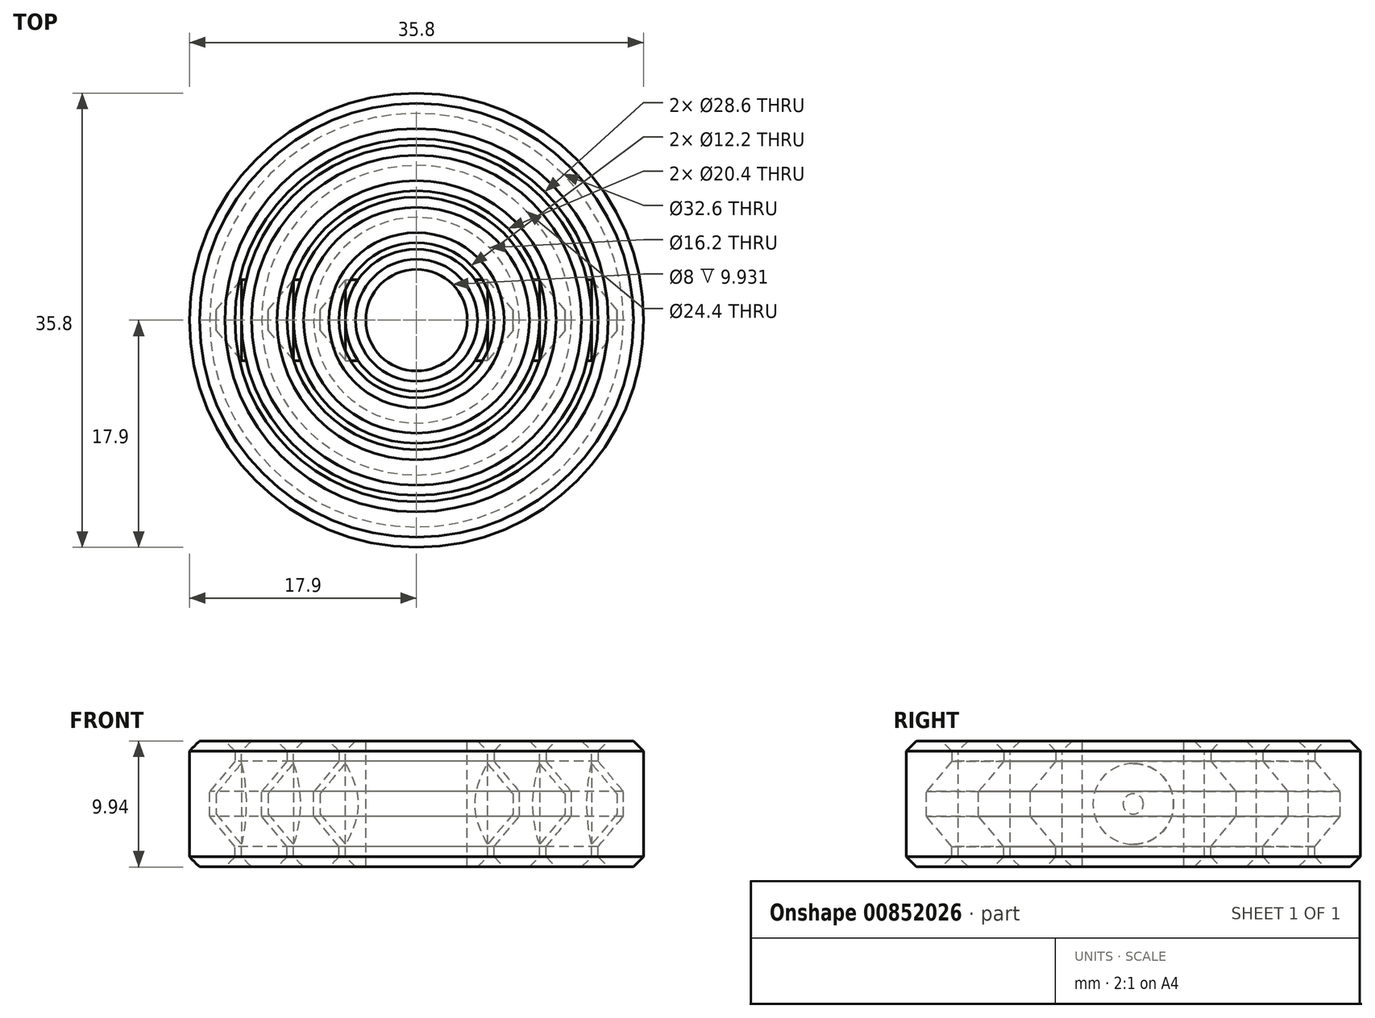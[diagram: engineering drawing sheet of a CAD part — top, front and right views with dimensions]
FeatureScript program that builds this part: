
annotation { "Feature Type Name" : "Feature", "Feature Type Description" : "" }
export const myFeature = defineFeature(function(context is Context, id is Id, definition is map)
    precondition{}
    {
        {
            assignVariable(context, id + "F0", {"name" : "Extrusion", "anyValue" : 0.4});
        }
        {
            assignVariable(context, id + "F1", {"name" : "Shells", "anyValue" : 2});
        }
        {
            assignVariable(context, id + "F2", {"name" : "MinStruct", "anyValue" : getVariable(context, 'Extrusion') * getVariable(context, 'Shells')});
        }
        {
            var Q0;
            Q0=qCreatedBy(makeId("Front.planeOp"),FACE);
            var sketch = newSketch(context, id + "F3", { "sketchPlane" : qUnion([Q0])});
            skLineSegment(sketch, "E0", {"start": v(0, 0) * mm, "end": v(0, -4.97) * mm});
            skLineSegment(sketch, "E1", {"start": v(0, -4.97) * mm, "end": v(5.6, -4.97) * mm});
            skLineSegment(sketch, "E2", {"start": v(5.6, -4.97) * mm, "end": v(5.6, 0) * mm});
            skLineSegment(sketch, "E3", {"start": v(5.6, 0) * mm, "end": v(0, 0) * mm});
            skLineSegment(sketch, "E4", {"start": v(5.6, -3.18) * mm, "end": v(7.6, -0.8) * mm});
            skLineSegment(sketch, "E5", {"start": v(7.6, -0.8) * mm, "end": v(7.6, 0) * mm});
            skLineSegment(sketch, "E6", {"start": v(7.6, 0) * mm, "end": v(5.6, 0) * mm});
            skLineSegment(sketch, "E7", {"start": v(6.1, -4.97) * mm, "end": v(6.1, -3.37) * mm});
            skLineSegment(sketch, "E8", {"start": v(6.1, -3.37) * mm, "end": v(8.1, -0.98) * mm});
            skLineSegment(sketch, "E9", {"start": v(8.1, -0.98) * mm, "end": v(8.1, 0) * mm});
            skLineSegment(sketch, "E10", {"start": v(8.1, 0) * mm, "end": v(9.7, 0) * mm});
            skLineSegment(sketch, "E11", {"start": v(9.7, 0) * mm, "end": v(9.7, -4.97) * mm});
            skLineSegment(sketch, "E12", {"start": v(9.7, -4.97) * mm, "end": v(6.1, -4.97) * mm});
            skLineSegment(sketch, "E13", {"start": v(4, -4.97) * mm, "end": v(4, 0) * mm});
            skLineSegment(sketch, "E14", {"start": v(9.7, -3.18) * mm, "end": v(11.7, -0.8) * mm});
            skLineSegment(sketch, "E15", {"start": v(11.7, -0.8) * mm, "end": v(11.7, 0) * mm});
            skLineSegment(sketch, "E16", {"start": v(11.7, 0) * mm, "end": v(9.7, 0) * mm});
            skArc(sketch, "E17", {"start": v(6.1, -7.54) * mm, "mid": v(8.75, -4.18) * mm, "end": v(9.7, 0) * mm});
            skPoint(sketch, "E18", {"position": v(6.1, -4.17) * mm});
            skArc(sketch, "E19", {"start": v(4, -3.92) * mm, "mid": v(5.18, -2.12) * mm, "end": v(5.6, 0) * mm});
            skLineSegment(sketch, "E20", {"start": v(5.6, -3.18) * mm, "end": v(4, -3.18) * mm});
            skLineSegment(sketch, "E21", {"start": v(9.7, -3.18) * mm, "end": v(9.16, -3.18) * mm});
            skLineSegment(sketch, "E22.1.0.0", {"start": v(15.8, 0) * mm, "end": v(13.8, 0) * mm});
            skLineSegment(sketch, "E22.1.0.1", {"start": v(15.8, -0.8) * mm, "end": v(15.8, 0) * mm});
            skLineSegment(sketch, "E22.1.0.2", {"start": v(13.8, -3.18) * mm, "end": v(15.8, -0.8) * mm});
            skLineSegment(sketch, "E22.1.0.3", {"start": v(13.8, 0) * mm, "end": v(13.8, -4.97) * mm});
            skLineSegment(sketch, "E22.1.0.4", {"start": v(13.8, -4.97) * mm, "end": v(10.2, -4.97) * mm});
            skLineSegment(sketch, "E22.1.0.5", {"start": v(10.2, -4.97) * mm, "end": v(10.2, -3.37) * mm});
            skLineSegment(sketch, "E22.1.0.6", {"start": v(10.2, -3.37) * mm, "end": v(12.2, -0.98) * mm});
            skLineSegment(sketch, "E22.1.0.7", {"start": v(12.2, -0.98) * mm, "end": v(12.2, 0) * mm});
            skLineSegment(sketch, "E22.1.0.8", {"start": v(12.2, 0) * mm, "end": v(13.8, 0) * mm});
            skLineSegment(sketch, "E22.2.0.0", {"start": v(19.9, 0) * mm, "end": v(17.9, 0) * mm});
            skLineSegment(sketch, "E22.2.0.1", {"start": v(19.9, -0.8) * mm, "end": v(19.9, 0) * mm});
            skLineSegment(sketch, "E22.2.0.2", {"start": v(17.9, -3.18) * mm, "end": v(19.9, -0.8) * mm});
            skLineSegment(sketch, "E22.2.0.3", {"start": v(17.9, 0) * mm, "end": v(17.9, -4.97) * mm});
            skLineSegment(sketch, "E22.2.0.4", {"start": v(17.9, -4.97) * mm, "end": v(14.3, -4.97) * mm});
            skLineSegment(sketch, "E22.2.0.5", {"start": v(14.3, -4.97) * mm, "end": v(14.3, -3.37) * mm});
            skLineSegment(sketch, "E22.2.0.6", {"start": v(14.3, -3.37) * mm, "end": v(16.3, -0.98) * mm});
            skLineSegment(sketch, "E22.2.0.7", {"start": v(16.3, -0.98) * mm, "end": v(16.3, 0) * mm});
            skLineSegment(sketch, "E22.2.0.8", {"start": v(16.3, 0) * mm, "end": v(17.9, 0) * mm});
            skLineSegment(sketch, "E22.direction1", {"start": v(6.1, -4.97) * mm, "end": v(10.2, -4.97) * mm, "construction": true});
            skArc(sketch, "E23", {"start": v(12.88, -4.97) * mm, "mid": v(13.57, -2.53) * mm, "end": v(13.8, 0) * mm});
            skArc(sketch, "E24", {"start": v(17.2, -4.97) * mm, "mid": v(17.72, -2.5) * mm, "end": v(17.9, 0) * mm});
            skLineSegment(sketch, "E25", {"start": v(13.8, -3.18) * mm, "end": v(13.43, -3.18) * mm});
            skLineSegment(sketch, "E26", {"start": v(17.9, -3.18) * mm, "end": v(17.61, -3.18) * mm});
            skSolve(sketch);
        }
        {
            var Q0;
            {var subQ5=sQuery(id+"F3.wireOp",EDGE,"E20");Q0=makeQuery(id+"F3.imprint","IMPRINT",FACE,{"disambiguationData":[TD([[makeQuery(id+"F3.imprint","IMPRINT",EDGE,{"derivedFrom":subQ5}),1.0]])]});}
            var Q1;
            {var subQ0=sQuery(id+"F3.wireOp",EDGE,"E19");Q1=makeQuery(id+"F3.imprint","IMPRINT",FACE,{"disambiguationData":[TD([[makeQuery(id+"F3.imprint","IMPRINT",EDGE,{"derivedFrom":subQ0}),-1.0]])]});}
            var Q2;
            {var subQ0=sQuery(id+"F3.wireOp",EDGE,"E19");Q2=makeQuery(id+"F3.imprint","IMPRINT",FACE,{"disambiguationData":[TD([[makeQuery(id+"F3.imprint","IMPRINT",EDGE,{"derivedFrom":subQ0}),1.0]])]});}
            var Q3;
            {var subQ5=sQuery(id+"F3.wireOp",EDGE,"E7");Q3=makeQuery(id+"F3.imprint","IMPRINT",FACE,{"disambiguationData":[TD([[makeQuery(id+"F3.imprint","IMPRINT",EDGE,{"derivedFrom":subQ5}),-1.0]])]});}
            var Q4;
            {var subQ3=sQuery(id+"F3.wireOp",EDGE,"E21");Q4=makeQuery(id+"F3.imprint","IMPRINT",FACE,{"disambiguationData":[TD([[makeQuery(id+"F3.imprint","IMPRINT",EDGE,{"derivedFrom":subQ3}),1.0]])]});}
            var Q5;
            {var subQ3=sQuery(id+"F3.wireOp",EDGE,"E21");Q5=makeQuery(id+"F3.imprint","IMPRINT",FACE,{"disambiguationData":[TD([[makeQuery(id+"F3.imprint","IMPRINT",EDGE,{"derivedFrom":subQ3}),-1.0]])]});}
            var Q6;
            {var subQ0=sQuery(id+"F3.wireOp",EDGE,"E22.1.0.5");Q6=makeQuery(id+"F3.imprint","IMPRINT",FACE,{"disambiguationData":[TD([[makeQuery(id+"F3.imprint","IMPRINT",EDGE,{"derivedFrom":subQ0}),-1.0]])]});}
            var Q7;
            {var subQ3=sQuery(id+"F3.wireOp",EDGE,"E25");Q7=makeQuery(id+"F3.imprint","IMPRINT",FACE,{"disambiguationData":[TD([[makeQuery(id+"F3.imprint","IMPRINT",EDGE,{"derivedFrom":subQ3}),-1.0]])]});}
            var Q8;
            {var subQ0=sQuery(id+"F3.wireOp",EDGE,"E25");Q8=makeQuery(id+"F3.imprint","IMPRINT",FACE,{"disambiguationData":[TD([[makeQuery(id+"F3.imprint","IMPRINT",EDGE,{"derivedFrom":subQ0}),1.0]])]});}
            var Q9;
            {var subQ0=sQuery(id+"F3.wireOp",EDGE,"E22.2.0.5");Q9=makeQuery(id+"F3.imprint","IMPRINT",FACE,{"disambiguationData":[TD([[makeQuery(id+"F3.imprint","IMPRINT",EDGE,{"derivedFrom":subQ0}),-1.0]])]});}
            var Q10;
            {var subQ3=sQuery(id+"F3.wireOp",EDGE,"E26");Q10=makeQuery(id+"F3.imprint","IMPRINT",FACE,{"disambiguationData":[TD([[makeQuery(id+"F3.imprint","IMPRINT",EDGE,{"derivedFrom":subQ3}),-1.0]])]});}
            var Q11;
            {var subQ0=sQuery(id+"F3.wireOp",EDGE,"E26");Q11=makeQuery(id+"F3.imprint","IMPRINT",FACE,{"disambiguationData":[TD([[makeQuery(id+"F3.imprint","IMPRINT",EDGE,{"derivedFrom":subQ0}),1.0]])]});}
            var Q12;
            {var subQ1=sQuery(id+"F3.wireOp",EDGE,"E3");var subQ3=sQuery(id+"F3.wireOp",EDGE,"E13");var subQ4=makeQuery(id+"F3.imprint","INTERSECT",VERTEX,{"derivedFrom":[subQ1,subQ3]});Q12=makeQuery(id+"F3.imprint","IMPRINT",FACE,{"disambiguationData":[TD([[makeQuery(id+"F3.imprint","IMPRINT",EDGE,{"disambiguationData":[TD([[subQ4,1.0]])],"derivedFrom":subQ3}),-1.0]])]});}
            var Q13;
            {var subQ5=sQuery(id+"F3.wireOp",EDGE,"E1");var subQ7=sQuery(id+"F3.wireOp",EDGE,"E2");var subQ8=makeQuery(id+"F3.imprint","INTERSECT",VERTEX,{"derivedFrom":[subQ5,subQ7]});Q13=makeQuery(id+"F3.imprint","IMPRINT",FACE,{"disambiguationData":[TD([[makeQuery(id+"F3.imprint","IMPRINT",EDGE,{"disambiguationData":[TD([[subQ8,1.0]])],"derivedFrom":subQ5}),1.0]])]});}
            var Q14;
            Q14=sQuery(id+"F3.wireOp",EDGE,"E0");
            revolve(context, id + "F4", {"surfaceOperationType" : NewSurfaceOperationType.NEW, "entities" : qUnion([Q0, Q1, Q2, Q3, Q4, Q5, Q6, Q7, Q8, Q9, Q10, Q11, Q12, Q13]), "axis" : qUnion([Q14]), "revolveType" : RevolveType.SYMMETRIC, "angle" : 180 * degree});
        }
        {
            var Q0;
            {var subQ2=sQuery(id+"F3.wireOp",EDGE,"E4");Q0=makeQuery(id+"F3.imprint","IMPRINT",FACE,{"disambiguationData":[TD([[makeQuery(id+"F3.imprint","IMPRINT",EDGE,{"derivedFrom":subQ2}),1.0]])]});}
            var Q1;
            {var subQ0=sQuery(id+"F3.wireOp",EDGE,"E19");Q1=makeQuery(id+"F3.imprint","IMPRINT",FACE,{"disambiguationData":[TD([[makeQuery(id+"F3.imprint","IMPRINT",EDGE,{"derivedFrom":subQ0}),-1.0]])]});}
            var Q2;
            {var subQ2=sQuery(id+"F3.wireOp",EDGE,"E14");Q2=makeQuery(id+"F3.imprint","IMPRINT",FACE,{"disambiguationData":[TD([[makeQuery(id+"F3.imprint","IMPRINT",EDGE,{"derivedFrom":subQ2}),1.0]])]});}
            var Q3;
            {var subQ3=sQuery(id+"F3.wireOp",EDGE,"E21");Q3=makeQuery(id+"F3.imprint","IMPRINT",FACE,{"disambiguationData":[TD([[makeQuery(id+"F3.imprint","IMPRINT",EDGE,{"derivedFrom":subQ3}),-1.0]])]});}
            var Q4;
            {var subQ0=sQuery(id+"F3.wireOp",EDGE,"E22.1.0.0");Q4=makeQuery(id+"F3.imprint","IMPRINT",FACE,{"disambiguationData":[TD([[makeQuery(id+"F3.imprint","IMPRINT",EDGE,{"derivedFrom":subQ0}),1.0]])]});}
            var Q5;
            {var subQ3=sQuery(id+"F3.wireOp",EDGE,"E25");Q5=makeQuery(id+"F3.imprint","IMPRINT",FACE,{"disambiguationData":[TD([[makeQuery(id+"F3.imprint","IMPRINT",EDGE,{"derivedFrom":subQ3}),-1.0]])]});}
            var Q6;
            Q6=sQuery(id+"F3.wireOp",EDGE,"E10");
            revolve(context, id + "F5", {"operationType" : NewBodyOperationType.ADD, "surfaceOperationType" : NewSurfaceOperationType.NEW, "entities" : qUnion([Q0, Q1, Q2, Q3, Q4, Q5]), "axis" : qUnion([Q6]), "revolveType" : RevolveType.SYMMETRIC, "angle" : 180 * degree});
        }
        {
            var Q0;
            Q0=makeQuery(id+"F4.opRevolve","SWEPT_EDGE",EDGE,{"disambiguationData":[OSD([sQuery(id+"F3.wireOp",EDGE,"E22.1.0.4"),sQuery(id+"F3.wireOp",EDGE,"E22.1.0.5")])]});
            var Q1;
            Q1=makeQuery(id+"F4.opRevolve","SWEPT_EDGE",EDGE,{"disambiguationData":[OSD([sQuery(id+"F3.wireOp",EDGE,"E22.2.0.4"),sQuery(id+"F3.wireOp",EDGE,"E22.2.0.5")])]});
            var Q2;
            Q2=makeQuery(id+"F4.opRevolve","SWEPT_EDGE",EDGE,{"disambiguationData":[OSD([sQuery(id+"F3.wireOp",EDGE,"E22.2.0.3"),sQuery(id+"F3.wireOp",EDGE,"E22.2.0.4")])]});
            var Q3;
            Q3=makeQuery(id+"F4.opRevolve","SWEPT_EDGE",EDGE,{"disambiguationData":[OSD([sQuery(id+"F3.wireOp",EDGE,"E11"),sQuery(id+"F3.wireOp",EDGE,"E12")])]});
            var Q4;
            Q4=makeQuery(id+"F4.opRevolve","SWEPT_EDGE",EDGE,{"disambiguationData":[OSD([sQuery(id+"F3.wireOp",EDGE,"E7"),sQuery(id+"F3.wireOp",EDGE,"E12")])]});
            var Q5;
            Q5=makeQuery(id+"F4.opRevolve","SWEPT_EDGE",EDGE,{"disambiguationData":[OSD([sQuery(id+"F3.wireOp",EDGE,"E1"),sQuery(id+"F3.wireOp",EDGE,"E2")])]});
            var Q6;
            Q6=makeQuery(id+"F4.opRevolve","SWEPT_EDGE",EDGE,{"disambiguationData":[OSD([sQuery(id+"F3.wireOp",EDGE,"E22.1.0.3"),sQuery(id+"F3.wireOp",EDGE,"E22.1.0.4")])]});
            chamfer(context, id + "F6", {"entities" : qUnion([Q0, Q1, Q2, Q3, Q4, Q5, Q6]), "width" : (getVariable(context, 'MinStruct')) * mm, "tangentPropagation" : true});
        }
        {
            var Q0;
            Q0=makeQuery(id+"F4.opRevolve","SWEPT_BODY",BODY,{"disambiguationData":[OSD([sQuery(id+"F3.wireOp",EDGE,"E1"),sQuery(id+"F3.wireOp",EDGE,"E2"),sQuery(id+"F3.wireOp",EDGE,"E3"),sQuery(id+"F3.wireOp",EDGE,"E13")])]});
            var Q1;
            Q1=makeQuery(id+"F4.opRevolve","SWEPT_BODY",BODY,{"disambiguationData":[OSD([sQuery(id+"F3.wireOp",EDGE,"E7"),sQuery(id+"F3.wireOp",EDGE,"E8"),sQuery(id+"F3.wireOp",EDGE,"E9"),sQuery(id+"F3.wireOp",EDGE,"E10"),sQuery(id+"F3.wireOp",EDGE,"E11"),sQuery(id+"F3.wireOp",EDGE,"E12")])]});
            var Q2;
            Q2=makeQuery(id+"F4.opRevolve","SWEPT_BODY",BODY,{"disambiguationData":[OSD([sQuery(id+"F3.wireOp",EDGE,"E22.1.0.3"),sQuery(id+"F3.wireOp",EDGE,"E22.1.0.4"),sQuery(id+"F3.wireOp",EDGE,"E22.1.0.5"),sQuery(id+"F3.wireOp",EDGE,"E22.1.0.6"),sQuery(id+"F3.wireOp",EDGE,"E22.1.0.7"),sQuery(id+"F3.wireOp",EDGE,"E22.1.0.8")])]});
            var Q3;
            Q3=makeQuery(id+"F4.opRevolve","SWEPT_BODY",BODY,{"disambiguationData":[OSD([sQuery(id+"F3.wireOp",EDGE,"E22.2.0.3"),sQuery(id+"F3.wireOp",EDGE,"E22.2.0.4"),sQuery(id+"F3.wireOp",EDGE,"E22.2.0.5"),sQuery(id+"F3.wireOp",EDGE,"E22.2.0.6"),sQuery(id+"F3.wireOp",EDGE,"E22.2.0.7"),sQuery(id+"F3.wireOp",EDGE,"E22.2.0.8")])]});
            var Q4;
            Q4=makeQuery(id+"F5.boolean.opBoolean","MERGE",FACE,{"derivedFrom":[makeQuery(id+"F4.opRevolve","SWEPT_FACE",FACE,{"disambiguationData":[OSD([sQuery(id+"F3.wireOp",EDGE,"E3")])]}),makeQuery(id+"F5.opRevolve","CAP_FACE",FACE,{"disambiguationData":[OSD([sQuery(id+"F3.wireOp",EDGE,"E4"),sQuery(id+"F3.wireOp",EDGE,"E5"),sQuery(id+"F3.wireOp",EDGE,"E6"),sQuery(id+"F3.wireOp",EDGE,"E19"),sQuery(id+"F3.wireOp",EDGE,"E20")])],"isStart":true})]});
            mirror(context, id + "F7", {"operationType" : NewBodyOperationType.ADD, "entities" : qUnion([Q0, Q1, Q2, Q3]), "mirrorPlane" : qUnion([Q4])});
        }
        {
            var Q0;
            Q0=makeQuery(id+"F4.opRevolve","SWEPT_BODY",BODY,{"disambiguationData":[OSD([sQuery(id+"F3.wireOp",EDGE,"E22.2.0.3"),sQuery(id+"F3.wireOp",EDGE,"E22.2.0.4"),sQuery(id+"F3.wireOp",EDGE,"E22.2.0.5"),sQuery(id+"F3.wireOp",EDGE,"E22.2.0.6"),sQuery(id+"F3.wireOp",EDGE,"E22.2.0.7"),sQuery(id+"F3.wireOp",EDGE,"E22.2.0.8")])]});
            var Q1;
            Q1=makeQuery(id+"F4.opRevolve","SWEPT_BODY",BODY,{"disambiguationData":[OSD([sQuery(id+"F3.wireOp",EDGE,"E22.1.0.3"),sQuery(id+"F3.wireOp",EDGE,"E22.1.0.4"),sQuery(id+"F3.wireOp",EDGE,"E22.1.0.5"),sQuery(id+"F3.wireOp",EDGE,"E22.1.0.6"),sQuery(id+"F3.wireOp",EDGE,"E22.1.0.7"),sQuery(id+"F3.wireOp",EDGE,"E22.1.0.8")])]});
            var Q2;
            Q2=makeQuery(id+"F4.opRevolve","SWEPT_BODY",BODY,{"disambiguationData":[OSD([sQuery(id+"F3.wireOp",EDGE,"E7"),sQuery(id+"F3.wireOp",EDGE,"E8"),sQuery(id+"F3.wireOp",EDGE,"E9"),sQuery(id+"F3.wireOp",EDGE,"E10"),sQuery(id+"F3.wireOp",EDGE,"E11"),sQuery(id+"F3.wireOp",EDGE,"E12")])]});
            var Q3;
            Q3=makeQuery(id+"F4.opRevolve","SWEPT_BODY",BODY,{"disambiguationData":[OSD([sQuery(id+"F3.wireOp",EDGE,"E1"),sQuery(id+"F3.wireOp",EDGE,"E2"),sQuery(id+"F3.wireOp",EDGE,"E3"),sQuery(id+"F3.wireOp",EDGE,"E13")])]});
            var Q4;
            {var subQ0=makeQuery(id+"F4.opRevolve","CAP_FACE",FACE,{"disambiguationData":[OSD([sQuery(id+"F3.wireOp",EDGE,"E1"),sQuery(id+"F3.wireOp",EDGE,"E2"),sQuery(id+"F3.wireOp",EDGE,"E3"),sQuery(id+"F3.wireOp",EDGE,"E13")])],"isStart":true});Q4=makeQuery(id+"F7.boolean.opBoolean","MERGE",FACE,{"derivedFrom":[subQ0,makeQuery(id+"F7.opPattern","COPY",FACE,{"derivedFrom":subQ0,"instanceName":"1"})]});}
            mirror(context, id + "F8", {"operationType" : NewBodyOperationType.ADD, "entities" : qUnion([Q0, Q1, Q2, Q3]), "mirrorPlane" : qUnion([Q4])});
        }
    });
